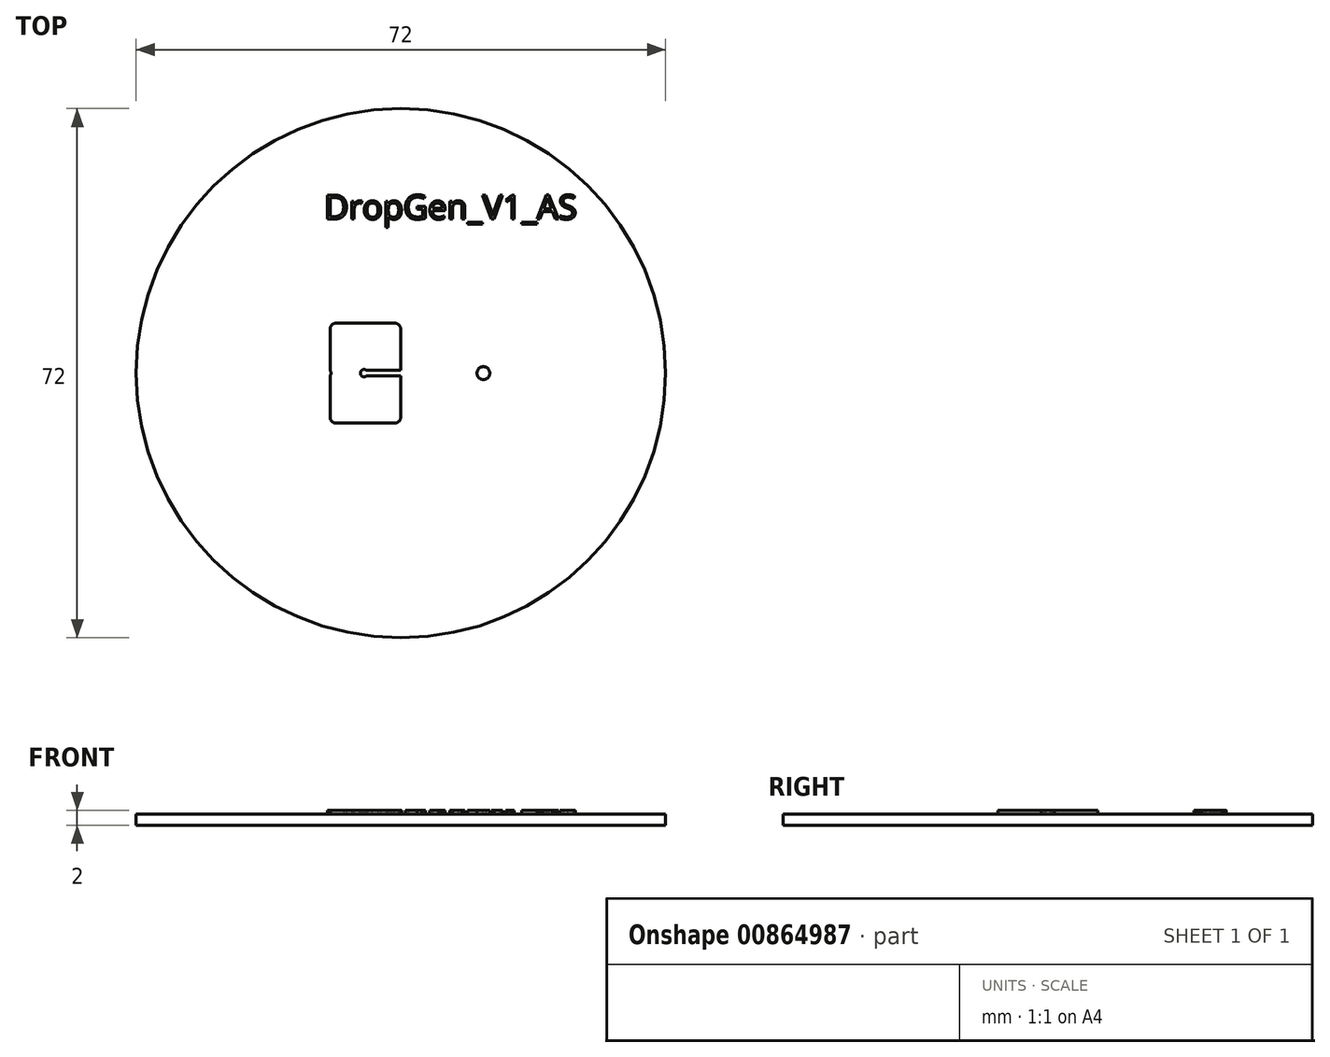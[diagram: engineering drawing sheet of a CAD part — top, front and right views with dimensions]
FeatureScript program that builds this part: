
annotation { "Feature Type Name" : "Feature", "Feature Type Description" : "" }
export const myFeature = defineFeature(function(context is Context, id is Id, definition is map)
    precondition{}
    {
        {
            var Q0;
            Q0=qCreatedBy(makeId("Top.planeOp"),FACE);
            var sketch = newSketch(context, id + "F0", { "sketchPlane" : qUnion([Q0])});
            skPoint(sketch, "E0.middle", {"position": v(0, 0) * mm});
            skLineSegment(sketch, "E1", {"start": v(-25, 0) * mm, "end": v(25, 0) * mm, "construction": true});
            skCircle(sketch, "E2", {"center": v(-10, 0) * mm, "radius": 0.5 * mm, "construction": true});
            skCircle(sketch, "E3", {"center": v(-10, 0) * mm, "radius": 0.38 * mm, "construction": true});
            skLineSegment(sketch, "E4", {"start": v(-9.62, 0) * mm, "end": v(-9.62, 6) * mm, "construction": true});
            skLineSegment(sketch, "E5", {"start": v(-10.37, 0) * mm, "end": v(-10.37, 6) * mm, "construction": true});
            skLineSegment(sketch, "E6", {"start": v(-9.62, 0) * mm, "end": v(-9.62, -6) * mm, "construction": true});
            skLineSegment(sketch, "E7", {"start": v(-10.37, 0) * mm, "end": v(-10.37, -6) * mm, "construction": true});
            skLineSegment(sketch, "E8", {"start": v(-9.62, 6) * mm, "end": v(-8.82, 6) * mm, "construction": true});
            skLineSegment(sketch, "E9", {"start": v(-8.82, 6) * mm, "end": v(-8.82, 6.8) * mm, "construction": true});
            skArc(sketch, "E10", {"start": v(-9.62, 6) * mm, "mid": v(-9.4, 6.57) * mm, "end": v(-8.82, 6.8) * mm});
            skArc(sketch, "E11", {"start": v(-10.37, 6) * mm, "mid": v(-9.92, 7.1) * mm, "end": v(-8.82, 7.55) * mm});
            skLineSegment(sketch, "E12", {"start": v(-8.82, 6.8) * mm, "end": v(-0.82, 6.8) * mm});
            skLineSegment(sketch, "E13", {"start": v(-8.82, 7.55) * mm, "end": v(-0.82, 7.55) * mm});
            skLineSegment(sketch, "E14", {"start": v(-0.82, 6.8) * mm, "end": v(-0.82, 6) * mm, "construction": true});
            skLineSegment(sketch, "E15", {"start": v(-0.82, 6) * mm, "end": v(-0.02, 6) * mm, "construction": true});
            skArc(sketch, "E16", {"start": v(-0.82, 6.8) * mm, "mid": v(-0.26, 6.57) * mm, "end": v(-0.02, 6) * mm});
            skArc(sketch, "E17", {"start": v(-0.82, 7.55) * mm, "mid": v(0.27, 7.1) * mm, "end": v(0.73, 6) * mm});
            skLineSegment(sketch, "E18.MirrorCS", {"start": v(-8.82, -7.55) * mm, "end": v(-0.82, -7.55) * mm});
            skLineSegment(sketch, "E19.MirrorCS", {"start": v(-8.82, -6.8) * mm, "end": v(-0.82, -6.8) * mm});
            skArc(sketch, "E20.MirrorCS", {"start": v(-10.37, -6) * mm, "mid": v(-9.92, -7.1) * mm, "end": v(-8.82, -7.55) * mm});
            skArc(sketch, "E21.MirrorCS", {"start": v(-9.62, -6) * mm, "mid": v(-9.4, -6.57) * mm, "end": v(-8.82, -6.8) * mm});
            skArc(sketch, "E22.MirrorCS", {"start": v(-0.82, -6.8) * mm, "mid": v(-0.26, -6.57) * mm, "end": v(-0.02, -6) * mm});
            skArc(sketch, "E23.MirrorCS", {"start": v(-0.82, -7.55) * mm, "mid": v(0.27, -7.1) * mm, "end": v(0.73, -6) * mm});
            skLineSegment(sketch, "E24", {"start": v(-0.02, 6) * mm, "end": v(-0.02, 0) * mm, "construction": true});
            skCircle(sketch, "E25", {"center": v(-5, 0) * mm, "radius": 0.5 * mm, "construction": true});
            skCircle(sketch, "E26", {"center": v(-5, 0) * mm, "radius": 0.38 * mm, "construction": true});
            skLineSegment(sketch, "E27", {"start": v(-5, 0) * mm, "end": v(-5, 0.38) * mm, "construction": true});
            skLineSegment(sketch, "E28", {"start": v(-5, 0) * mm, "end": v(-5, -0.38) * mm, "construction": true});
            skLineSegment(sketch, "E29", {"start": v(-5, 0.38) * mm, "end": v(-0.02, 0.38) * mm, "construction": true});
            skLineSegment(sketch, "E30.MirrorCS", {"start": v(-5, -0.38) * mm, "end": v(-0.02, -0.38) * mm, "construction": true});
            skLineSegment(sketch, "E31", {"start": v(-0.02, 6) * mm, "end": v(-0.02, 0.38) * mm});
            skLineSegment(sketch, "E32", {"start": v(-0.02, -0.38) * mm, "end": v(-0.02, -6) * mm});
            skLineSegment(sketch, "E33", {"start": v(0.73, 6) * mm, "end": v(0.73, 0.38) * mm});
            skLineSegment(sketch, "E34", {"start": v(0.73, -6) * mm, "end": v(0.73, -0.38) * mm});
            skLineSegment(sketch, "E35", {"start": v(0.73, 0.38) * mm, "end": v(1.23, 0.38) * mm, "construction": true});
            skLineSegment(sketch, "E36", {"start": v(0.73, 0.38) * mm, "end": v(1.23, 0.87) * mm});
            skLineSegment(sketch, "E37.MirrorCS", {"start": v(0.73, -0.38) * mm, "end": v(1.23, -0.87) * mm});
            skLineSegment(sketch, "E38", {"start": v(1.23, -0.87) * mm, "end": v(11.23, -0.87) * mm});
            skLineSegment(sketch, "E39.MirrorCS", {"start": v(1.23, 0.87) * mm, "end": v(11.23, 0.87) * mm});
            skLineSegment(sketch, "E40", {"start": v(11.23, 0.87) * mm, "end": v(11.23, -0.87) * mm, "construction": true});
            skCircle(sketch, "E41", {"center": v(11.23, 0) * mm, "radius": 0.87 * mm});
            skLineSegment(sketch, "E42", {"start": v(-4.67, -0.38) * mm, "end": v(-0.02, -0.38) * mm});
            skLineSegment(sketch, "E43.MirrorCS", {"start": v(-4.67, 0.38) * mm, "end": v(-0.02, 0.38) * mm});
            skArc(sketch, "E44", {"start": v(-4.67, 0.38) * mm, "mid": v(-5.5, 0) * mm, "end": v(-4.67, -0.38) * mm});
            skArc(sketch, "E45", {"start": v(-10.37, -0.33) * mm, "mid": v(-10.5, 0) * mm, "end": v(-10.37, 0.33) * mm});
            skArc(sketch, "E46", {"start": v(-9.62, -0.33) * mm, "mid": v(-9.5, 0) * mm, "end": v(-9.62, 0.33) * mm});
            skLineSegment(sketch, "E47", {"start": v(-9.62, 0.33) * mm, "end": v(-9.62, 6) * mm});
            skLineSegment(sketch, "E48", {"start": v(-10.37, 0.33) * mm, "end": v(-10.37, 6) * mm});
            skLineSegment(sketch, "E49", {"start": v(-9.62, -0.33) * mm, "end": v(-9.62, -6) * mm});
            skLineSegment(sketch, "E50", {"start": v(-10.37, -0.33) * mm, "end": v(-10.37, -6) * mm});
            skText(sketch, "E51", { "text": "DropGen_V1_AS", "fontName": "OpenSans-Regular.ttf"});
            skCircle(sketch, "E52", {"center": v(0, 0) * mm, "radius": 36 * mm});
            const initialGuessF0  = {"E51": [-0.01045, 0.02095, 1, 0, 0.0033]};
            skSetInitialGuess(sketch, initialGuessF0);
            skSolve(sketch);
        }
        {
            var Q0;
            Q0 = qSketchRegion(id + "F0", true);
            var Q1;
            Q1=makeQuery(id+"F0.imprint","IMPRINT",FACE,{"disambiguationData":[TD([[makeQuery(id+"F0.imprint","IMPRINT",EDGE,{"derivedFrom":sQuery(id+"F0.wireOp",EDGE,"E11")}),1.0]])]});
            var Q2;
            Q2=makeQuery(id+"F0.imprint","IMPRINT",FACE,{"disambiguationData":[TD([[makeQuery(id+"F0.imprint","IMPRINT",EDGE,{"derivedFrom":sQuery(id+"F0.wireOp",EDGE,"E51.sketch_text.stroke-129")}),-1.0]])]});
            var Q3;
            Q3=makeQuery(id+"F0.imprint","IMPRINT",FACE,{"disambiguationData":[TD([[makeQuery(id+"F0.imprint","IMPRINT",EDGE,{"derivedFrom":sQuery(id+"F0.wireOp",EDGE,"E10")}),1.0]])]});
            var Q4;
            Q4=makeQuery(id+"F0.imprint","IMPRINT",FACE,{"disambiguationData":[TD([[makeQuery(id+"F0.imprint","IMPRINT",EDGE,{"derivedFrom":sQuery(id+"F0.wireOp",EDGE,"E51.sketch_text.stroke-69")}),-1.0]])]});
            var Q5;
            Q5=makeQuery(id+"F0.imprint","IMPRINT",FACE,{"disambiguationData":[TD([[makeQuery(id+"F0.imprint","IMPRINT",EDGE,{"derivedFrom":sQuery(id+"F0.wireOp",EDGE,"E51.sketch_text.stroke-147")}),-1.0]])]});
            var Q6;
            Q6=makeQuery(id+"F0.imprint","IMPRINT",FACE,{"disambiguationData":[TD([[makeQuery(id+"F0.imprint","IMPRINT",EDGE,{"derivedFrom":sQuery(id+"F0.wireOp",EDGE,"E51.sketch_text.stroke-138")}),-1.0]])]});
            var Q7;
            Q7=makeQuery(id+"F0.imprint","IMPRINT",FACE,{"disambiguationData":[TD([[makeQuery(id+"F0.imprint","IMPRINT",EDGE,{"derivedFrom":sQuery(id+"F0.wireOp",EDGE,"E51.sketch_text.stroke-108")}),-1.0]])]});
            var Q8;
            Q8=makeQuery(id+"F0.imprint","IMPRINT",FACE,{"disambiguationData":[TD([[makeQuery(id+"F0.imprint","IMPRINT",EDGE,{"derivedFrom":sQuery(id+"F0.wireOp",EDGE,"E51.sketch_text.stroke-125")}),-1.0]])]});
            var Q9;
            Q9=makeQuery(id+"F0.imprint","IMPRINT",FACE,{"disambiguationData":[TD([[makeQuery(id+"F0.imprint","IMPRINT",EDGE,{"derivedFrom":sQuery(id+"F0.wireOp",EDGE,"E51.sketch_text.stroke-44")}),-1.0]])]});
            var Q10;
            Q10=makeQuery(id+"F0.imprint","IMPRINT",FACE,{"disambiguationData":[TD([[makeQuery(id+"F0.imprint","IMPRINT",EDGE,{"derivedFrom":sQuery(id+"F0.wireOp",EDGE,"E51.sketch_text.stroke-0")}),-1.0]])]});
            var Q11;
            Q11=makeQuery(id+"F0.imprint","IMPRINT",FACE,{"disambiguationData":[TD([[makeQuery(id+"F0.imprint","IMPRINT",EDGE,{"derivedFrom":sQuery(id+"F0.wireOp",EDGE,"E51.sketch_text.stroke-7")}),1.0]])]});
            var Q12;
            {var subQ0=sQuery(id+"F0.wireOp",EDGE,"E41");var subQ1=makeQuery(id+"F0.imprint","INTERSECT",VERTEX,{"derivedFrom":[sQuery(id+"F0.wireOp",EDGE,"E38"),subQ0]});Q12=makeQuery(id+"F0.imprint","IMPRINT",FACE,{"disambiguationData":[TD([[makeQuery(id+"F0.imprint","IMPRINT",EDGE,{"disambiguationData":[TD([[subQ1,1.0]])],"derivedFrom":subQ0}),1.0]])]});}
            var Q13;
            Q13=makeQuery(id+"F0.imprint","IMPRINT",FACE,{"disambiguationData":[TD([[makeQuery(id+"F0.imprint","IMPRINT",EDGE,{"derivedFrom":sQuery(id+"F0.wireOp",EDGE,"E51.sketch_text.stroke-36")}),1.0]])]});
            var Q14;
            Q14=makeQuery(id+"F0.imprint","IMPRINT",FACE,{"disambiguationData":[TD([[makeQuery(id+"F0.imprint","IMPRINT",EDGE,{"derivedFrom":sQuery(id+"F0.wireOp",EDGE,"E51.sketch_text.stroke-164")}),-1.0]])]});
            var Q15;
            Q15=makeQuery(id+"F0.imprint","IMPRINT",FACE,{"disambiguationData":[TD([[makeQuery(id+"F0.imprint","IMPRINT",EDGE,{"derivedFrom":sQuery(id+"F0.wireOp",EDGE,"E51.sketch_text.stroke-151")}),-1.0]])]});
            var Q16;
            Q16=makeQuery(id+"F0.imprint","IMPRINT",FACE,{"disambiguationData":[TD([[makeQuery(id+"F0.imprint","IMPRINT",EDGE,{"derivedFrom":sQuery(id+"F0.wireOp",EDGE,"E51.sketch_text.stroke-14")}),-1.0]])]});
            var Q17;
            Q17=makeQuery(id+"F0.imprint","IMPRINT",FACE,{"disambiguationData":[TD([[makeQuery(id+"F0.imprint","IMPRINT",EDGE,{"derivedFrom":sQuery(id+"F0.wireOp",EDGE,"E51.sketch_text.stroke-27")}),-1.0]])]});
            var Q18;
            Q18=makeQuery(id+"F0.imprint","IMPRINT",FACE,{"disambiguationData":[TD([[makeQuery(id+"F0.imprint","IMPRINT",EDGE,{"derivedFrom":sQuery(id+"F0.wireOp",EDGE,"E51.sketch_text.stroke-159")}),1.0]])]});
            var Q19;
            Q19=makeQuery(id+"F0.imprint","IMPRINT",FACE,{"disambiguationData":[TD([[makeQuery(id+"F0.imprint","IMPRINT",EDGE,{"derivedFrom":sQuery(id+"F0.wireOp",EDGE,"E51.sketch_text.stroke-89")}),-1.0]])]});
            var Q20;
            Q20=makeQuery(id+"F0.imprint","IMPRINT",FACE,{"disambiguationData":[TD([[makeQuery(id+"F0.imprint","IMPRINT",EDGE,{"derivedFrom":sQuery(id+"F0.wireOp",EDGE,"E51.sketch_text.stroke-103")}),1.0]])]});
            var Q21;
            Q21=makeQuery(id+"F0.imprint","IMPRINT",FACE,{"disambiguationData":[TD([[makeQuery(id+"F0.imprint","IMPRINT",EDGE,{"derivedFrom":sQuery(id+"F0.wireOp",EDGE,"E51.sketch_text.stroke-60")}),1.0]])]});
            var Q22;
            Q22=makeQuery(id+"F0.imprint","IMPRINT",FACE,{"disambiguationData":[TD([[makeQuery(id+"F0.imprint","IMPRINT",EDGE,{"derivedFrom":sQuery(id+"F0.wireOp",EDGE,"E10")}),-1.0]])]});
            extrude(context, id + "F1", {"entities" : qUnion([Q0, Q1, Q2, Q3, Q4, Q5, Q6, Q7, Q8, Q9, Q10, Q11, Q12, Q13, Q14, Q15, Q16, Q17, Q18, Q19, Q20, Q21, Q22]), "oppositeDirection" : true, "depth" : 1.5 * mm, "offsetDistance" : 25 * mm});
        }
        {
            var Q0;
            Q0=makeQuery(id+"F0.imprint","IMPRINT",FACE,{"disambiguationData":[TD([[makeQuery(id+"F0.imprint","IMPRINT",EDGE,{"derivedFrom":sQuery(id+"F0.wireOp",EDGE,"E10")}),1.0]])]});
            var Q1;
            {var subQ0=sQuery(id+"F0.wireOp",EDGE,"E41");var subQ1=makeQuery(id+"F0.imprint","INTERSECT",VERTEX,{"derivedFrom":[sQuery(id+"F0.wireOp",EDGE,"E38"),subQ0]});Q1=makeQuery(id+"F0.imprint","IMPRINT",FACE,{"disambiguationData":[TD([[makeQuery(id+"F0.imprint","IMPRINT",EDGE,{"disambiguationData":[TD([[subQ1,1.0]])],"derivedFrom":subQ0}),1.0]])]});}
            var Q2;
            Q2=makeQuery(id+"F0.imprint","IMPRINT",FACE,{"disambiguationData":[TD([[makeQuery(id+"F0.imprint","IMPRINT",EDGE,{"derivedFrom":sQuery(id+"F0.wireOp",EDGE,"E51.sketch_text.stroke-0")}),-1.0]])]});
            var Q3;
            Q3=makeQuery(id+"F0.imprint","IMPRINT",FACE,{"disambiguationData":[TD([[makeQuery(id+"F0.imprint","IMPRINT",EDGE,{"derivedFrom":sQuery(id+"F0.wireOp",EDGE,"E51.sketch_text.stroke-14")}),-1.0]])]});
            var Q4;
            Q4=makeQuery(id+"F0.imprint","IMPRINT",FACE,{"disambiguationData":[TD([[makeQuery(id+"F0.imprint","IMPRINT",EDGE,{"derivedFrom":sQuery(id+"F0.wireOp",EDGE,"E51.sketch_text.stroke-27")}),-1.0]])]});
            var Q5;
            Q5=makeQuery(id+"F0.imprint","IMPRINT",FACE,{"disambiguationData":[TD([[makeQuery(id+"F0.imprint","IMPRINT",EDGE,{"derivedFrom":sQuery(id+"F0.wireOp",EDGE,"E51.sketch_text.stroke-44")}),-1.0]])]});
            var Q6;
            Q6=makeQuery(id+"F0.imprint","IMPRINT",FACE,{"disambiguationData":[TD([[makeQuery(id+"F0.imprint","IMPRINT",EDGE,{"derivedFrom":sQuery(id+"F0.wireOp",EDGE,"E51.sketch_text.stroke-69")}),-1.0]])]});
            var Q7;
            Q7=makeQuery(id+"F0.imprint","IMPRINT",FACE,{"disambiguationData":[TD([[makeQuery(id+"F0.imprint","IMPRINT",EDGE,{"derivedFrom":sQuery(id+"F0.wireOp",EDGE,"E51.sketch_text.stroke-89")}),-1.0]])]});
            var Q8;
            Q8=makeQuery(id+"F0.imprint","IMPRINT",FACE,{"disambiguationData":[TD([[makeQuery(id+"F0.imprint","IMPRINT",EDGE,{"derivedFrom":sQuery(id+"F0.wireOp",EDGE,"E51.sketch_text.stroke-108")}),-1.0]])]});
            var Q9;
            Q9=makeQuery(id+"F0.imprint","IMPRINT",FACE,{"disambiguationData":[TD([[makeQuery(id+"F0.imprint","IMPRINT",EDGE,{"derivedFrom":sQuery(id+"F0.wireOp",EDGE,"E51.sketch_text.stroke-125")}),-1.0]])]});
            var Q10;
            Q10=makeQuery(id+"F0.imprint","IMPRINT",FACE,{"disambiguationData":[TD([[makeQuery(id+"F0.imprint","IMPRINT",EDGE,{"derivedFrom":sQuery(id+"F0.wireOp",EDGE,"E51.sketch_text.stroke-129")}),-1.0]])]});
            var Q11;
            Q11=makeQuery(id+"F0.imprint","IMPRINT",FACE,{"disambiguationData":[TD([[makeQuery(id+"F0.imprint","IMPRINT",EDGE,{"derivedFrom":sQuery(id+"F0.wireOp",EDGE,"E51.sketch_text.stroke-138")}),-1.0]])]});
            var Q12;
            Q12=makeQuery(id+"F0.imprint","IMPRINT",FACE,{"disambiguationData":[TD([[makeQuery(id+"F0.imprint","IMPRINT",EDGE,{"derivedFrom":sQuery(id+"F0.wireOp",EDGE,"E51.sketch_text.stroke-147")}),-1.0]])]});
            var Q13;
            Q13=makeQuery(id+"F0.imprint","IMPRINT",FACE,{"disambiguationData":[TD([[makeQuery(id+"F0.imprint","IMPRINT",EDGE,{"derivedFrom":sQuery(id+"F0.wireOp",EDGE,"E51.sketch_text.stroke-151")}),-1.0]])]});
            var Q14;
            Q14=makeQuery(id+"F0.imprint","IMPRINT",FACE,{"disambiguationData":[TD([[makeQuery(id+"F0.imprint","IMPRINT",EDGE,{"derivedFrom":sQuery(id+"F0.wireOp",EDGE,"E51.sketch_text.stroke-164")}),-1.0]])]});
            extrude(context, id + "F2", {"entities" : qUnion([Q0, Q1, Q2, Q3, Q4, Q5, Q6, Q7, Q8, Q9, Q10, Q11, Q12, Q13, Q14]), "operationType" : NewBodyOperationType.ADD, "depth" : 0.5 * mm, "offsetDistance" : 25 * mm});
        }
    });
